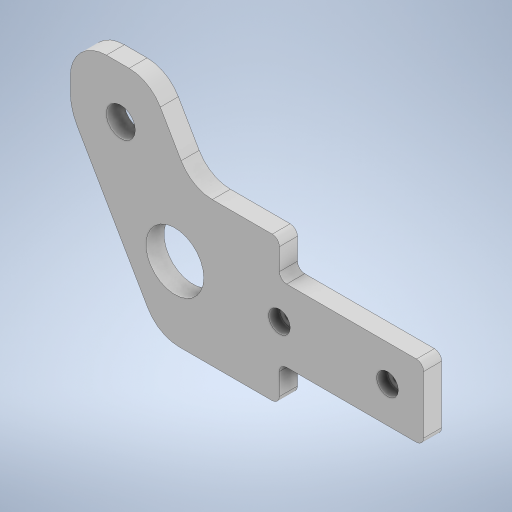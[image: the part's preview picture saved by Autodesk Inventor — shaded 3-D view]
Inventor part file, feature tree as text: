
AUTODESK INVENTOR PART (.ipt)
format: ipt  version: 2024.3 (Build 283343000, 343)  size: 300,544 bytes
history: native  units: mm
features: sketch x3, extrude x2, fillet x2, other x1, hole x1
ambient origin geometry x8: Origin, YZ Plane, XZ Plane, XY Plane, X Axis, Y Axis, Z Axis, Center Point
bodies: Body1 (feature_tree)
feature tree (9):
  other  "ソリッド1"
  extrude  "押し出し1"  Depth=98.0mm
  hole  "穴1"  [1 undecoded]
  fillet  "フィレット1"  Radius=40.0mm
  fillet  "フィレット2"  Radius=20.0mm
  extrude  "押し出し2"  Depth=10.0mm
  sketch  "スケッチ1"
  sketch  "スケッチ2"
  sketch  "スケッチ4"
note: 1 required parameter value undecoded (feature->parameter linkage not recoverable at this tier; creation-order binding heuristic only, values carry confidence <= 0.55)
